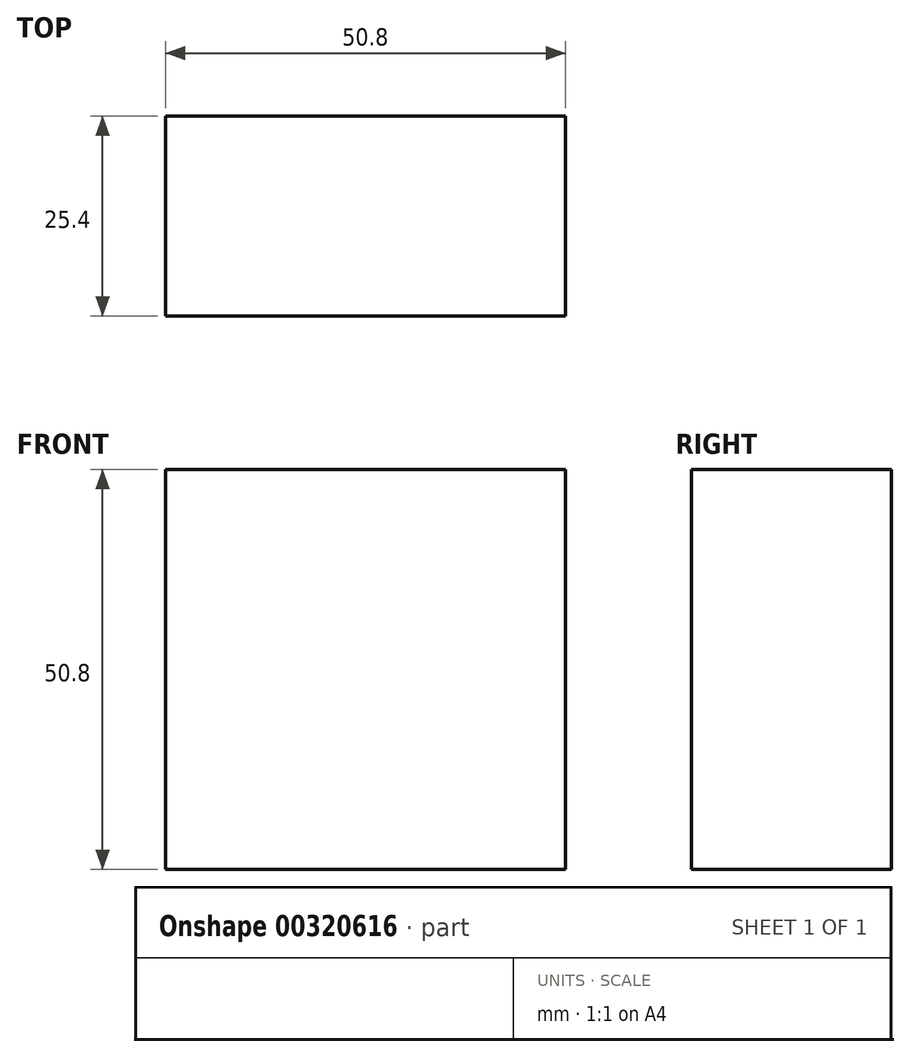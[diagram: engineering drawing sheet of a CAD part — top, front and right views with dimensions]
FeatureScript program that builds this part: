
annotation { "Feature Type Name" : "Feature", "Feature Type Description" : "" }
export const myFeature = defineFeature(function(context is Context, id is Id, definition is map)
    precondition{}
    {
        {
            var Q0;
            Q0=qCreatedBy(makeId("Front.planeOp"),FACE);
            var sketch = newSketch(context, id + "F0", { "sketchPlane" : qUnion([Q0])});
            skLineSegment(sketch, "E0.bottom", {"start": v(25.4, 25.4) * mm, "end": v(-25.4, 25.4) * mm});
            skLineSegment(sketch, "E0.top", {"start": v(25.4, -25.4) * mm, "end": v(-25.4, -25.4) * mm});
            skLineSegment(sketch, "E0.left", {"start": v(25.4, 25.4) * mm, "end": v(25.4, -25.4) * mm});
            skLineSegment(sketch, "E0.right", {"start": v(-25.4, 25.4) * mm, "end": v(-25.4, -25.4) * mm});
            skPoint(sketch, "E0.middle", {"position": v(0, 0) * mm});
            skSolve(sketch);
        }
        {
            var Q0;
            Q0 = qSketchRegion(id + "F0", true);
            extrude(context, id + "F1", {"entities" : qUnion([Q0]), "depth" : 25.4 * mm});
        }
    });
